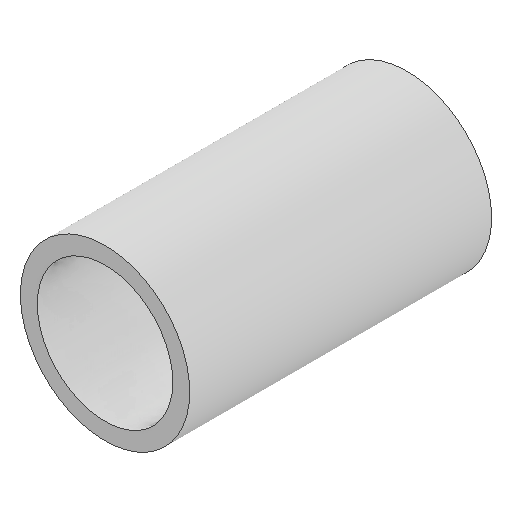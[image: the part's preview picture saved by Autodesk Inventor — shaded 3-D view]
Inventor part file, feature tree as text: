
AUTODESK INVENTOR PART (.ipt)
format: ipt  version: 2025.1 (Build 291241000, 241)  size: 103,424 bytes
history: native  units: mm
features: other x1, extrude x1, sketch x1
ambient origin geometry x8: Origin, YZ Plane, XZ Plane, XY Plane, X Axis, Y Axis, Z Axis, Center Point
bodies: Body1 (feature_tree)
feature tree (3):
  other  "Bryła1"
  extrude  "Wyciągnięcie proste1"  Depth=3.6mm
  sketch  "Szkic1"
